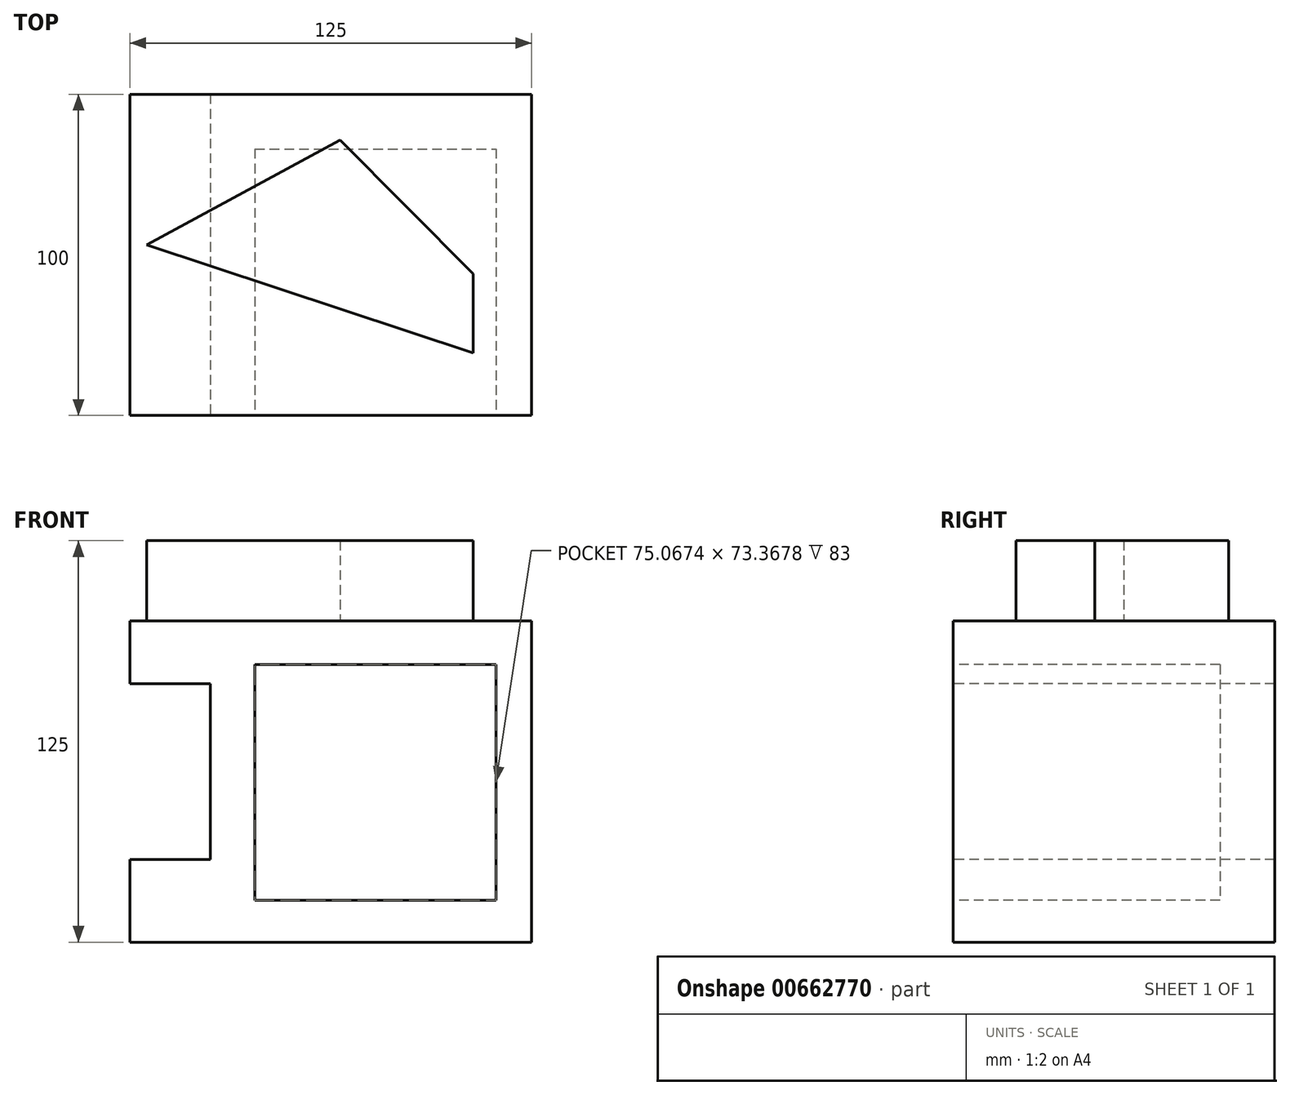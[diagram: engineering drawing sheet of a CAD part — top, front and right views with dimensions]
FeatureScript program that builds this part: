
annotation { "Feature Type Name" : "Feature", "Feature Type Description" : "" }
export const myFeature = defineFeature(function(context is Context, id is Id, definition is map)
    precondition{}
    {
        {
            var Q0;
            Q0=qCreatedBy(makeId("Front.planeOp"),FACE);
            var sketch = newSketch(context, id + "F0", { "sketchPlane" : qUnion([Q0])});
            skLineSegment(sketch, "E0.bottom", {"start": v(-32.15, 61.33) * mm, "end": v(67.85, 61.33) * mm});
            skLineSegment(sketch, "E0.top", {"start": v(-32.15, -38.67) * mm, "end": v(67.85, -38.67) * mm});
            skLineSegment(sketch, "E0.left", {"start": v(-32.15, 61.33) * mm, "end": v(-32.15, -38.67) * mm});
            skLineSegment(sketch, "E0.right", {"start": v(67.85, 61.33) * mm, "end": v(67.85, -38.67) * mm});
            skSolve(sketch);
        }
        {
            var Q0;
            Q0=makeQuery(id+"F0.imprint","IMPRINT",FACE,{"disambiguationData":[TD([[makeQuery(id+"F0.imprint","IMPRINT",EDGE,{"derivedFrom":sQuery(id+"F0.wireOp",EDGE,"E0.bottom")}),-1.0]])]});
            extrude(context, id + "F1", {"entities" : qUnion([Q0]), "depth" : 100 * mm, "offsetDistance" : 25 * mm});
        }
        {
            var Q0;
            Q0=makeQuery(id+"F1.opExtrude","CAP_FACE",FACE,{"disambiguationData":[OSD([sQuery(id+"F0.wireOp",EDGE,"E0.bottom"),sQuery(id+"F0.wireOp",EDGE,"E0.top"),sQuery(id+"F0.wireOp",EDGE,"E0.left"),sQuery(id+"F0.wireOp",EDGE,"E0.right")])],"isStart":false});
            var sketch = newSketch(context, id + "F2", { "sketchPlane" : qUnion([Q0])});
            skLineSegment(sketch, "E1.bottom", {"start": v(-18.27, 47.73) * mm, "end": v(56.8, 47.73) * mm});
            skLineSegment(sketch, "E1.top", {"start": v(-18.27, -25.64) * mm, "end": v(56.8, -25.64) * mm});
            skLineSegment(sketch, "E1.left", {"start": v(-18.27, 47.73) * mm, "end": v(-18.27, -25.64) * mm});
            skLineSegment(sketch, "E1.right", {"start": v(56.8, 47.73) * mm, "end": v(56.8, -25.64) * mm});
            skSolve(sketch);
        }
        {
            var Q0;
            Q0 = qSketchRegion(id + "F2", true);
            extrude(context, id + "F3", {"entities" : qUnion([Q0]), "operationType" : NewBodyOperationType.REMOVE, "oppositeDirection" : true, "depth" : 83 * mm, "offsetDistance" : 25 * mm});
        }
        {
            var Q0;
            Q0=makeQuery(id+"F1.opExtrude","SWEPT_FACE",FACE,{"disambiguationData":[OSD([sQuery(id+"F0.wireOp",EDGE,"E0.left")])]});
            var sketch = newSketch(context, id + "F4", { "sketchPlane" : qUnion([Q0])});
            skLineSegment(sketch, "E2.bottom", {"start": v(0, -12.89) * mm, "end": v(100, -12.89) * mm});
            skLineSegment(sketch, "E2.top", {"start": v(0, -38.67) * mm, "end": v(100, -38.67) * mm});
            skLineSegment(sketch, "E2.left", {"start": v(0, -12.89) * mm, "end": v(0, -38.67) * mm});
            skLineSegment(sketch, "E2.right", {"start": v(100, -12.89) * mm, "end": v(100, -38.67) * mm});
            skSolve(sketch);
        }
        {
            var Q0;
            Q0 = qSketchRegion(id + "F4", true);
            extrude(context, id + "F5", {"entities" : qUnion([Q0]), "operationType" : NewBodyOperationType.ADD, "depth" : 25 * mm, "offsetDistance" : 25 * mm});
        }
        {
            var Q0;
            Q0=makeQuery(id+"F1.opExtrude","SWEPT_FACE",FACE,{"disambiguationData":[OSD([sQuery(id+"F0.wireOp",EDGE,"E0.left")])]});
            var sketch = newSketch(context, id + "F6", { "sketchPlane" : qUnion([Q0])});
            skLineSegment(sketch, "E3.bottom", {"start": v(0, 61.33) * mm, "end": v(100, 61.33) * mm});
            skLineSegment(sketch, "E3.top", {"start": v(0, 41.78) * mm, "end": v(100, 41.78) * mm});
            skLineSegment(sketch, "E3.left", {"start": v(0, 61.33) * mm, "end": v(0, 41.78) * mm});
            skLineSegment(sketch, "E3.right", {"start": v(100, 61.33) * mm, "end": v(100, 41.78) * mm});
            skSolve(sketch);
        }
        {
            var Q0;
            Q0 = qSketchRegion(id + "F6", true);
            extrude(context, id + "F7", {"entities" : qUnion([Q0]), "operationType" : NewBodyOperationType.ADD, "depth" : 25 * mm, "offsetDistance" : 25 * mm});
        }
        {
            var Q0;
            Q0=makeQuery(id+"F7.boolean.opBoolean","MERGE",FACE,{"derivedFrom":[makeQuery(id+"F1.opExtrude","SWEPT_FACE",FACE,{"disambiguationData":[OSD([sQuery(id+"F0.wireOp",EDGE,"E0.bottom")])]}),makeQuery(id+"F7.opExtrude","SWEPT_FACE",FACE,{"disambiguationData":[OSD([sQuery(id+"F6.wireOp",EDGE,"E3.bottom")])]})]});
            var sketch = newSketch(context, id + "F8", { "sketchPlane" : qUnion([Q0])});
            skLineSegment(sketch, "E4", {"start": v(-51.98, -46.92) * mm, "end": v(49.62, -80.53) * mm});
            skLineSegment(sketch, "E5", {"start": v(8.2, -14.3) * mm, "end": v(49.62, -55.92) * mm});
            skLineSegment(sketch, "E6", {"start": v(49.62, -80.53) * mm, "end": v(49.62, -55.92) * mm});
            skLineSegment(sketch, "E7", {"start": v(8.2, -14.3) * mm, "end": v(-51.98, -46.92) * mm});
            skSolve(sketch);
        }
        {
            var Q0;
            Q0 = qSketchRegion(id + "F8", true);
            extrude(context, id + "F9", {"entities" : qUnion([Q0]), "operationType" : NewBodyOperationType.ADD, "depth" : 25 * mm, "offsetDistance" : 25 * mm});
        }
        {
            var Q0;
            Q0=makeQuery(id+"F5.boolean.opBoolean","MERGE",FACE,{"derivedFrom":[makeQuery(id+"F1.opExtrude","SWEPT_FACE",FACE,{"disambiguationData":[OSD([sQuery(id+"F0.wireOp",EDGE,"E0.top")])]}),makeQuery(id+"F5.opExtrude","SWEPT_FACE",FACE,{"disambiguationData":[OSD([sQuery(id+"F4.wireOp",EDGE,"E2.top")])]})]});
            var sketch = newSketch(context, id + "F10", { "sketchPlane" : qUnion([Q0])});
            skLineSegment(sketch, "E8", {"start": v(-52.07, 47.83) * mm, "end": v(49.53, 14.22) * mm});
            skLineSegment(sketch, "E9", {"start": v(8.11, 80.46) * mm, "end": v(49.53, 38.84) * mm});
            skLineSegment(sketch, "E10", {"start": v(49.53, 14.22) * mm, "end": v(49.53, 38.84) * mm});
            skLineSegment(sketch, "E11", {"start": v(8.11, 80.46) * mm, "end": v(-52.07, 47.83) * mm});
            skSolve(sketch);
        }
        {
            var Q0;
            Q0 = qConstructionFilter(qBodyType(qCreatedBy(id + "F10" ,EDGE), BodyType.WIRE), ConstructionObject.NO);
            extrude(context, id + "F11", {"bodyType" : ToolBodyType.SURFACE, "surfaceEntities" : qUnion([Q0]), "depth" : 25 * mm, "offsetDistance" : 25 * mm});
        }
    });
